# Revit family: Tub_Spout-Grohe-Concetto-13274_Series
name_source: partatom
category: Plumbing Fixtures
revit_build: Autodesk Revit 2018 (Build: 20170223_1515(x64)
units: mm (PartAtom-declared; Revit-internal decimal feet)

## family parameters
Cut with Voids When Loaded = No
Host = Face
OmniClass Number = 23.45.05.14.21.11
OmniClass Title = Bath/Shower Units
Part Type = Normal
Room Calculation Point = No
Round Connector Dimension = Use Diameter
Shared = Yes

## types (5) — shared parameters
ADA Compliant = Yes
Assembly Code = D2020300
CWFU = 3
Default Elevation = 21"
Description = Concetto Tub Spout
Diameter = 3 1/8"
HWFU = 3
Installation Type = Wall Mounted
Manufacturer = Grohe
Overall Length = 7 3/8"
Price = Prices may vary. Please consult Manufacturer Representative for most up-to-date price list.
Product Documentation Link = https://americanstandard.box.com
Product Page URL = https://www.grohe.us
Revised Date = 05/26/2021
Spout Reach = 6 11/16"
Tempered Connection Diameter = 1/2"
Tempered Connection Radius = 1/4"
URL = https://www.grohe.us
Warranty Documentation Link = https://cdn.cloud.grohe.com
cUPC Compliant = Yes
zero-valued in all types: WFU

## per-type parameters (varying)
| type | Finish | Material |
| 13274A01 | Metal-Grohe-A01-Hard Graphite | Metal-Grohe-A01-Hard Graphite |
| 13274BE1 | Metal-Grohe-BE1-Polished Nickel Infinity Finish | Metal-Grohe-BE1-Polished Nickel Infinity Finish |
| 13274GN1 | Metal-Grohe-GN1-Brushed Cool Sunrise | Metal-Grohe-GN1-Brushed Cool Sunrise |
| 13274001 | Metal-Grohe-001-StarLight Chrome | Metal-Grohe-001-StarLight Chrome |
| 13274EN1 | Metal-Grohe-EN1-Brushed Nickel Infinity Finish | Metal-Grohe-EN1-Brushed Nickel Infinity Finish |

note: column(s) folded — value = type name in every type: Model

## geometry (parser evidence)
native form markers: Sweep x3
no freeform markers — native parametric forms only
